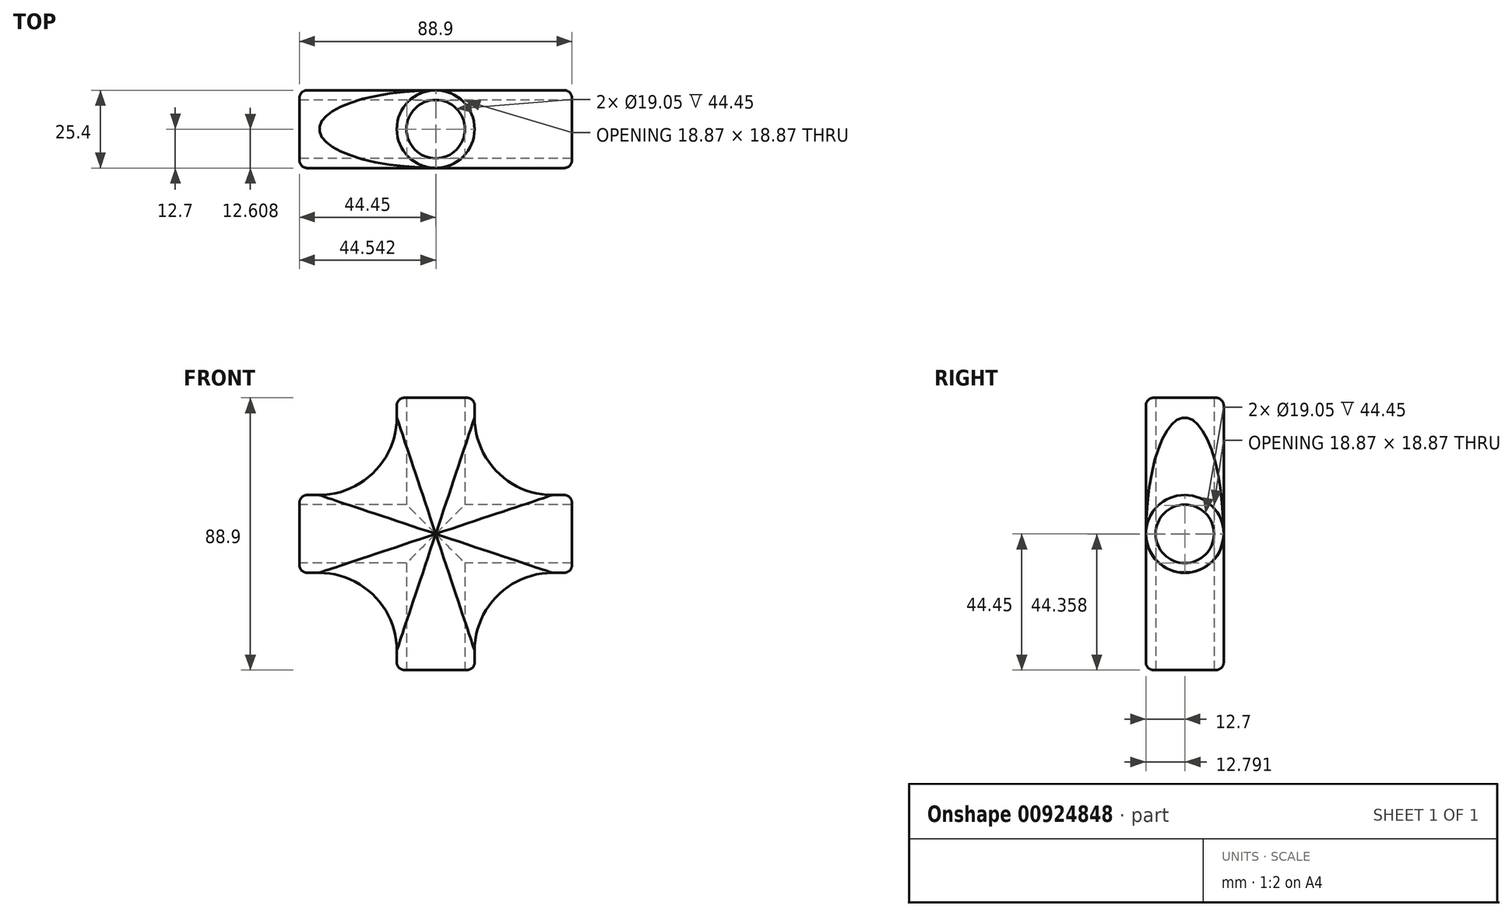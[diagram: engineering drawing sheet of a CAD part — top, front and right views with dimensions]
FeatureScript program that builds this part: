
annotation { "Feature Type Name" : "Feature", "Feature Type Description" : "" }
export const myFeature = defineFeature(function(context is Context, id is Id, definition is map)
    precondition{}
    {
        {
            var Q0;
            Q0=qCreatedBy(makeId("Top.planeOp"),FACE);
            var sketch = newSketch(context, id + "F0", { "sketchPlane" : qUnion([Q0])});
            skCircle(sketch, "E0", {"center": v(0, 0) * mm, "radius": 12.7 * mm});
            skCircle(sketch, "E1", {"center": v(0, 0) * mm, "radius": 9.53 * mm});
            skSolve(sketch);
        }
        {
            var Q0;
            Q0 = qSketchRegion(id + "F0", true);
            extrude(context, id + "F1", {"entities" : qUnion([Q0]), "depth" : 44.45 * mm, "offsetDistance" : 25.4 * mm, "hasSecondDirection" : true, "secondDirectionOppositeDirection" : true, "secondDirectionDepth" : 44.45 * mm});
        }
        {
            var Q0;
            Q0=qCreatedBy(makeId("Right.planeOp"),FACE);
            var sketch = newSketch(context, id + "F2", { "sketchPlane" : qUnion([Q0])});
            skCircle(sketch, "E2", {"center": v(0, 0) * mm, "radius": 12.7 * mm});
            skCircle(sketch, "E3", {"center": v(0, 0) * mm, "radius": 9.53 * mm});
            skSolve(sketch);
        }
        {
            var Q0;
            Q0 = qSketchRegion(id + "F2", true);
            extrude(context, id + "F3", {"entities" : qUnion([Q0]), "operationType" : NewBodyOperationType.ADD, "depth" : 44.45 * mm, "offsetDistance" : 25.4 * mm, "hasSecondDirection" : true, "secondDirectionOppositeDirection" : true, "secondDirectionDepth" : 44.45 * mm});
        }
        {
            var Q0;
            Q0=qCreatedBy(makeId("Top.planeOp"),FACE);
            var sketch = newSketch(context, id + "F4", { "sketchPlane" : qUnion([Q0])});
            skCircle(sketch, "E4", {"center": v(0, 0) * mm, "radius": 9.53 * mm});
            skSolve(sketch);
        }
        {
            var Q0;
            Q0 = qSketchRegion(id + "F4", true);
            extrude(context, id + "F5", {"entities" : qUnion([Q0]), "operationType" : NewBodyOperationType.REMOVE, "oppositeDirection" : true, "depth" : 25.4 * mm, "offsetDistance" : 25.4 * mm, "hasSecondDirection" : true, "secondDirectionOppositeDirection" : false, "secondDirectionDepth" : 25.4 * mm});
        }
        {
            var Q0;
            Q0=qCreatedBy(makeId("Right.planeOp"),FACE);
            var sketch = newSketch(context, id + "F6", { "sketchPlane" : qUnion([Q0])});
            skCircle(sketch, "E5", {"center": v(0, 0) * mm, "radius": 9.53 * mm});
            skSolve(sketch);
        }
        {
            var Q0;
            Q0 = qSketchRegion(id + "F6", true);
            extrude(context, id + "F7", {"entities" : qUnion([Q0]), "operationType" : NewBodyOperationType.REMOVE, "oppositeDirection" : true, "depth" : 25.4 * mm, "offsetDistance" : 25.4 * mm, "hasSecondDirection" : true, "secondDirectionOppositeDirection" : false, "secondDirectionDepth" : 25.4 * mm});
        }
        {
            var Q0;
            Q0=makeQuery(id+"F3.boolean.opBoolean","INTERSECT",EDGE,{"disambiguationData":[OD(3.0)],"derivedFrom":[makeQuery(id+"F1.opExtrude","SWEPT_FACE",FACE,{"disambiguationData":[OSD([sQuery(id+"F0.wireOp",EDGE,"E0")])]}),makeQuery(id+"F3.opExtrude","SWEPT_FACE",FACE,{"disambiguationData":[OSD([sQuery(id+"F2.wireOp",EDGE,"E2")])]})]});
            var Q1;
            Q1=makeQuery(id+"F3.boolean.opBoolean","INTERSECT",EDGE,{"disambiguationData":[OD(1.0)],"derivedFrom":[makeQuery(id+"F1.opExtrude","SWEPT_FACE",FACE,{"disambiguationData":[OSD([sQuery(id+"F0.wireOp",EDGE,"E0")])]}),makeQuery(id+"F3.opExtrude","SWEPT_FACE",FACE,{"disambiguationData":[OSD([sQuery(id+"F2.wireOp",EDGE,"E2")])]})]});
            var Q2;
            Q2=makeQuery(id+"F3.boolean.opBoolean","INTERSECT",EDGE,{"disambiguationData":[OD(2.0)],"derivedFrom":[makeQuery(id+"F1.opExtrude","SWEPT_FACE",FACE,{"disambiguationData":[OSD([sQuery(id+"F0.wireOp",EDGE,"E0")])]}),makeQuery(id+"F3.opExtrude","SWEPT_FACE",FACE,{"disambiguationData":[OSD([sQuery(id+"F2.wireOp",EDGE,"E2")])]})]});
            var Q3;
            Q3=makeQuery(id+"F3.boolean.opBoolean","INTERSECT",EDGE,{"disambiguationData":[OD(0.0)],"derivedFrom":[makeQuery(id+"F1.opExtrude","SWEPT_FACE",FACE,{"disambiguationData":[OSD([sQuery(id+"F0.wireOp",EDGE,"E0")])]}),makeQuery(id+"F3.opExtrude","SWEPT_FACE",FACE,{"disambiguationData":[OSD([sQuery(id+"F2.wireOp",EDGE,"E2")])]})]});
            fillet(context, id + "F8", {"entities" : qUnion([Q0, Q1, Q2, Q3]), "radius" : 25.4 * mm, "tangentPropagation" : true, "allowEdgeOverflow" : false});
        }
        {
            var Q0;
            Q0=makeQuery(id+"F1.opExtrude","CAP_EDGE",EDGE,{"disambiguationData":[OSD([sQuery(id+"F0.wireOp",EDGE,"E0")])],"isStart":false});
            var Q1;
            Q1=makeQuery(id+"F3.opExtrude","CAP_EDGE",EDGE,{"disambiguationData":[OSD([sQuery(id+"F2.wireOp",EDGE,"E2")])],"isStart":true});
            var Q2;
            Q2=makeQuery(id+"F3.opExtrude","CAP_EDGE",EDGE,{"disambiguationData":[OSD([sQuery(id+"F2.wireOp",EDGE,"E2")])],"isStart":false});
            var Q3;
            Q3=makeQuery(id+"F1.opExtrude","CAP_EDGE",EDGE,{"disambiguationData":[OSD([sQuery(id+"F0.wireOp",EDGE,"E0")])],"isStart":true});
            fillet(context, id + "F9", {"entities" : qUnion([Q0, Q1, Q2, Q3]), "radius" : 2.54 * mm, "tangentPropagation" : true, "allowEdgeOverflow" : false});
        }
    });
